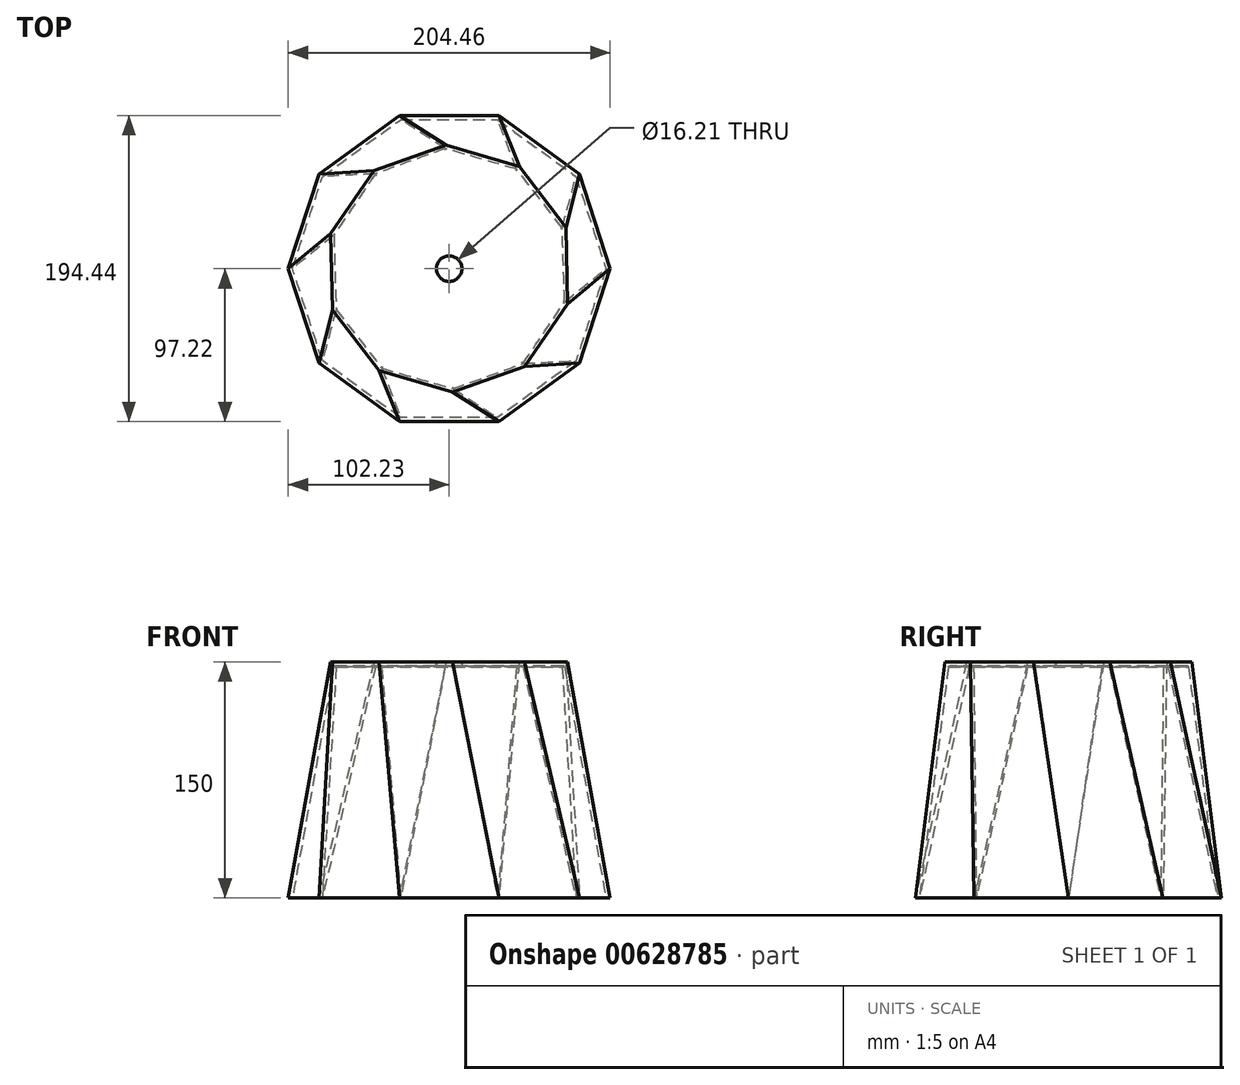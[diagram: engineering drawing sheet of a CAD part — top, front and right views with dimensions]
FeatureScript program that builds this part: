
annotation { "Feature Type Name" : "Feature", "Feature Type Description" : "" }
export const myFeature = defineFeature(function(context is Context, id is Id, definition is map)
    precondition{}
    {
        {
            var Q0;
            Q0=qCreatedBy(makeId("Top.planeOp"),FACE);
            var sketch = newSketch(context, id + "F0", { "sketchPlane" : qUnion([Q0])});
            skCircle(sketch, "E0.cCircle", {"center": v(0, 0) * mm, "radius": 74.7 * mm, "construction": true});
            skLineSegment(sketch, "E0.0", {"start": v(74.05, 26.17) * mm, "end": v(75.29, -22.36) * mm});
            skLineSegment(sketch, "E0.1", {"start": v(75.29, -22.36) * mm, "end": v(47.77, -62.34) * mm});
            skLineSegment(sketch, "E0.2", {"start": v(47.77, -62.34) * mm, "end": v(2, -78.5) * mm});
            skLineSegment(sketch, "E0.3", {"start": v(2, -78.5) * mm, "end": v(-44.53, -64.7) * mm});
            skLineSegment(sketch, "E0.4", {"start": v(-44.53, -64.7) * mm, "end": v(-74.05, -26.17) * mm});
            skLineSegment(sketch, "E0.5", {"start": v(-74.05, -26.17) * mm, "end": v(-75.29, 22.36) * mm});
            skLineSegment(sketch, "E0.6", {"start": v(-75.29, 22.36) * mm, "end": v(-47.77, 62.34) * mm});
            skLineSegment(sketch, "E0.7", {"start": v(-47.77, 62.34) * mm, "end": v(-2, 78.5) * mm});
            skLineSegment(sketch, "E0.8", {"start": v(-2, 78.5) * mm, "end": v(44.53, 64.7) * mm});
            skLineSegment(sketch, "E0.9", {"start": v(44.53, 64.7) * mm, "end": v(74.05, 26.17) * mm});
            skPoint(sketch, "E0.0.midPoint", {"position": v(74.67, 1.9) * mm});
            skSolve(sketch);
        }
        {
            var Q0;
            Q0=qCreatedBy(makeId("Top.planeOp"),FACE);
            cPlane(context, id + "F1", {"entities" : qUnion([Q0]), "cplaneType" : CPlaneType.OFFSET, "offset" : 150 * mm, "oppositeDirection" : true, "width" : 150 * mm, "height" : 150 * mm});
        }
        {
            var Q0;
            Q0=qCreatedBy(id+"F1.planeOp",FACE);
            var sketch = newSketch(context, id + "F2", { "sketchPlane" : qUnion([Q0])});
            skCircle(sketch, "E1.cCircle", {"center": v(0, 0) * mm, "radius": 97.22 * mm, "construction": true});
            skLineSegment(sketch, "E1.0", {"start": v(-31.59, 97.22) * mm, "end": v(31.59, 97.22) * mm});
            skLineSegment(sketch, "E1.1", {"start": v(31.59, 97.22) * mm, "end": v(82.7, 60.09) * mm});
            skLineSegment(sketch, "E1.2", {"start": v(82.7, 60.09) * mm, "end": v(102.23, 0) * mm});
            skLineSegment(sketch, "E1.3", {"start": v(102.23, 0) * mm, "end": v(82.7, -60.09) * mm});
            skLineSegment(sketch, "E1.4", {"start": v(82.7, -60.09) * mm, "end": v(31.59, -97.22) * mm});
            skLineSegment(sketch, "E1.5", {"start": v(31.59, -97.22) * mm, "end": v(-31.59, -97.22) * mm});
            skLineSegment(sketch, "E1.6", {"start": v(-31.59, -97.22) * mm, "end": v(-82.7, -60.09) * mm});
            skLineSegment(sketch, "E1.7", {"start": v(-82.7, -60.09) * mm, "end": v(-102.23, 0) * mm});
            skLineSegment(sketch, "E1.8", {"start": v(-102.23, 0) * mm, "end": v(-82.7, 60.09) * mm});
            skLineSegment(sketch, "E1.9", {"start": v(-82.7, 60.09) * mm, "end": v(-31.59, 97.22) * mm});
            skPoint(sketch, "E1.0.midPoint", {"position": v(0, 97.22) * mm});
            skSolve(sketch);
        }
        {
            var Q0;
            Q0=makeQuery(id+"F0.imprint","IMPRINT",FACE,{"disambiguationData":[TD([[makeQuery(id+"F0.imprint","IMPRINT",EDGE,{"derivedFrom":sQuery(id+"F0.wireOp",EDGE,"E0.0")}),-1.0]])]});
            var Q1;
            Q1=makeQuery(id+"F2.imprint","IMPRINT",FACE,{"disambiguationData":[TD([[makeQuery(id+"F2.imprint","IMPRINT",EDGE,{"derivedFrom":sQuery(id+"F2.wireOp",EDGE,"E1.0")}),-1.0]])]});
            loft(context, id + "F3", {"sheetProfilesArray" : [{ "sheetProfileEntities" : qUnion([Q0]) }, { "sheetProfileEntities" : qUnion([Q1]) }]});
        }
        {
            var Q0;
            Q0=makeQuery(id+"F3.opLoft","CAP_FACE",FACE,{"disambiguationData":[OSD([makeQuery(id+"F2.imprint","IMPRINT",FACE,{"disambiguationData":[TD([[makeQuery(id+"F2.imprint","IMPRINT",EDGE,{"derivedFrom":sQuery(id+"F2.wireOp",EDGE,"E1.0")}),-1.0]])]})])],"isStart":true});
            shell(context, id + "F4", {"entities" : qUnion([Q0]), "thickness" : 2.5 * mm});
        }
        {
            var Q0;
            Q0=qCreatedBy(makeId("Top.planeOp"),FACE);
            var sketch = newSketch(context, id + "F5", { "sketchPlane" : qUnion([Q0])});
            skCircle(sketch, "E2", {"center": v(0, 0) * mm, "radius": 8.1 * mm});
            skSolve(sketch);
        }
        {
            var Q0;
            Q0=makeQuery(id+"F5.imprint","IMPRINT",FACE,{"disambiguationData":[TD([[makeQuery(id+"F5.imprint","IMPRINT",EDGE,{"derivedFrom":sQuery(id+"F5.wireOp",EDGE,"E2")}),1.0]])]});
            extrude(context, id + "F6", {"entities" : qUnion([Q0]), "operationType" : NewBodyOperationType.REMOVE, "oppositeDirection" : true, "depth" : 20 * mm, "offsetDistance" : 25 * mm});
        }
        {
            var Q0;
            Q0=makeQuery(id+"F4.opShell","OFFSET_FACE",FACE,{"disambiguationData":[OSD([makeQuery(id+"F0.imprint","IMPRINT",FACE,{"disambiguationData":[TD([[makeQuery(id+"F0.imprint","IMPRINT",EDGE,{"derivedFrom":sQuery(id+"F0.wireOp",EDGE,"E0.0")}),-1.0]])]})])]});
            fillet(context, id + "F7", {"entities" : qUnion([Q0]), "radius" : 1 * mm, "tangentPropagation" : true, "allowEdgeOverflow" : false});
        }
    });
